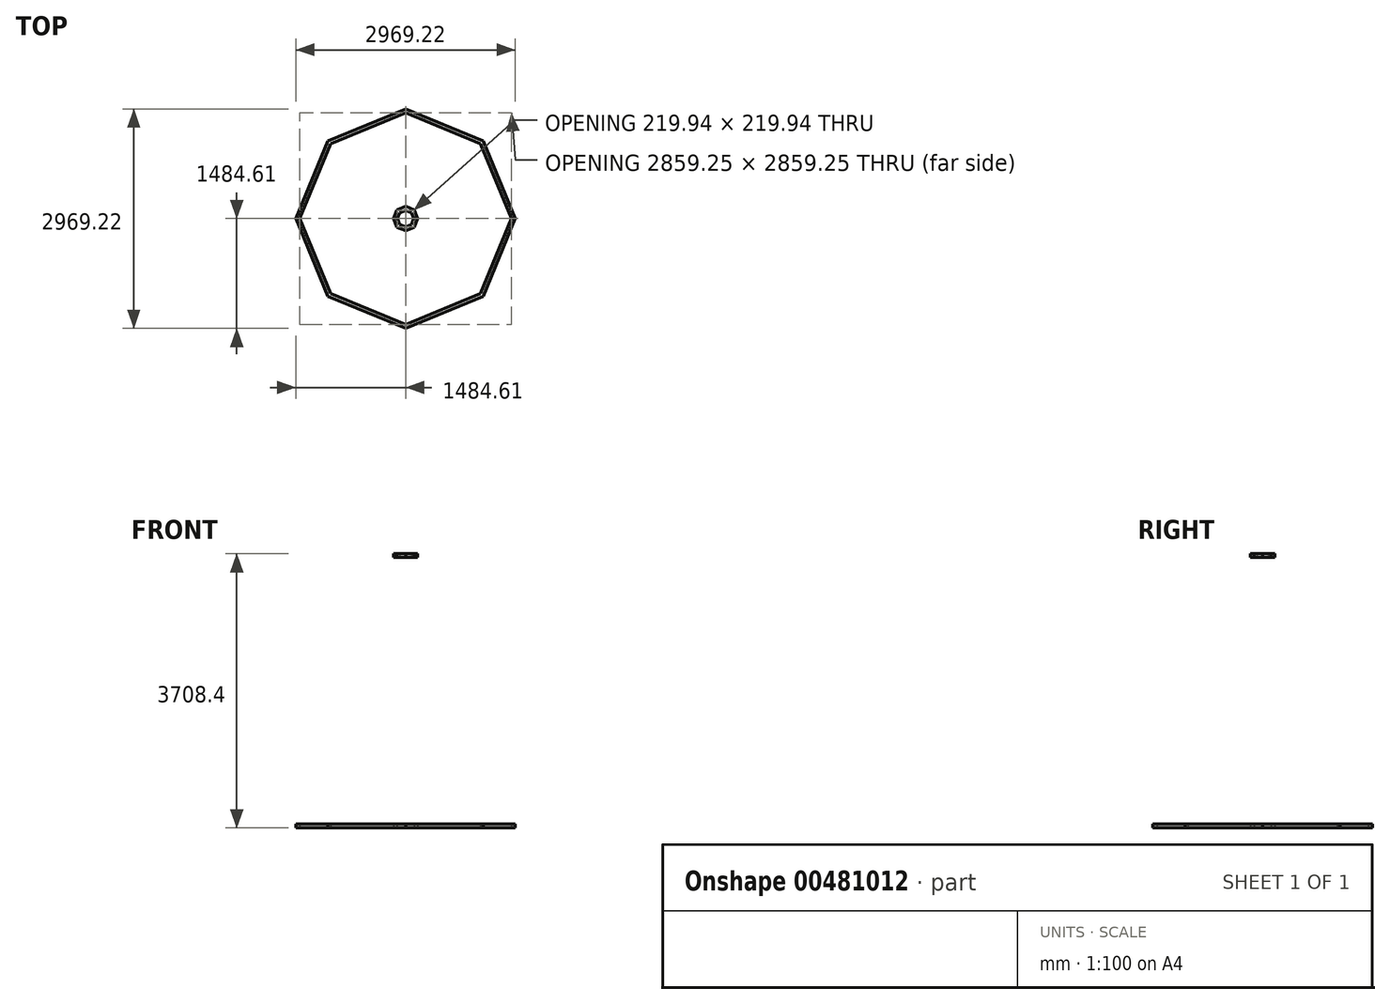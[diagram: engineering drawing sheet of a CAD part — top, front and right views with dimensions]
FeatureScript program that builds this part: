
annotation { "Feature Type Name" : "Feature", "Feature Type Description" : "" }
export const myFeature = defineFeature(function(context is Context, id is Id, definition is map)
    precondition{}
    {
        {
            var Q0;
            Q0=qCreatedBy(makeId("Top.planeOp"),FACE);
            var sketch = newSketch(context, id + "F0", { "sketchPlane" : qUnion([Q0])});
            skCircle(sketch, "E0.cCircle", {"center": v(0, 0) * mm, "radius": 1371.6 * mm, "construction": true});
            skLineSegment(sketch, "E0.0", {"start": v(1484.6, 0) * mm, "end": v(1049.78, -1049.78) * mm});
            skLineSegment(sketch, "E0.1", {"start": v(1049.78, -1049.78) * mm, "end": v(0, -1484.6) * mm});
            skLineSegment(sketch, "E0.2", {"start": v(0, -1484.6) * mm, "end": v(-1049.78, -1049.78) * mm});
            skLineSegment(sketch, "E0.3", {"start": v(-1049.78, -1049.78) * mm, "end": v(-1484.6, 0) * mm});
            skLineSegment(sketch, "E0.4", {"start": v(-1484.6, 0) * mm, "end": v(-1049.78, 1049.78) * mm});
            skLineSegment(sketch, "E0.5", {"start": v(-1049.78, 1049.78) * mm, "end": v(0, 1484.6) * mm});
            skLineSegment(sketch, "E0.6", {"start": v(0, 1484.6) * mm, "end": v(1049.78, 1049.78) * mm});
            skLineSegment(sketch, "E0.7", {"start": v(1049.78, 1049.78) * mm, "end": v(1484.6, 0) * mm});
            skPoint(sketch, "E0.0.midPoint", {"position": v(1267.2, -524.89) * mm});
            skLineSegment(sketch, "E1.0", {"start": v(-1429.62, 0) * mm, "end": v(-1010.9, 1010.9) * mm});
            skLineSegment(sketch, "E1.1", {"start": v(-1010.9, -1010.9) * mm, "end": v(-1429.62, 0) * mm});
            skLineSegment(sketch, "E1.2", {"start": v(-1010.9, 1010.9) * mm, "end": v(0, 1429.62) * mm});
            skLineSegment(sketch, "E1.3", {"start": v(0, -1429.62) * mm, "end": v(-1010.9, -1010.9) * mm});
            skLineSegment(sketch, "E1.4", {"start": v(0, 1429.62) * mm, "end": v(1010.9, 1010.9) * mm});
            skLineSegment(sketch, "E1.5", {"start": v(1010.9, 1010.9) * mm, "end": v(1429.62, 0) * mm});
            skLineSegment(sketch, "E1.6", {"start": v(1429.62, 0) * mm, "end": v(1010.9, -1010.9) * mm});
            skLineSegment(sketch, "E1.7", {"start": v(1010.9, -1010.9) * mm, "end": v(0, -1429.62) * mm});
            skSolve(sketch);
        }
        {
            var Q0;
            Q0 = qSketchRegion(id + "F0", true);
            extrude(context, id + "F1", {"entities" : qUnion([Q0]), "depth" : 50.8 * mm});
        }
        {
            var Q0;
            Q0=qCreatedBy(makeId("Top.planeOp"),FACE);
            cPlane(context, id + "F2", {"entities" : qUnion([Q0]), "cplaneType" : CPlaneType.OFFSET, "offset" : 3657.6 * mm, "width" : 152.4 * mm, "height" : 152.4 * mm});
        }
        {
            var Q0;
            Q0=qCreatedBy(id+"F2.planeOp",FACE);
            var sketch = newSketch(context, id + "F3", { "sketchPlane" : qUnion([Q0])});
            skCircle(sketch, "E2.cCircle", {"center": v(0, 0) * mm, "radius": 152.4 * mm, "construction": true});
            skLineSegment(sketch, "E2.0", {"start": v(164.96, 0) * mm, "end": v(116.64, -116.64) * mm});
            skLineSegment(sketch, "E2.1", {"start": v(116.64, -116.64) * mm, "end": v(0, -164.96) * mm});
            skLineSegment(sketch, "E2.2", {"start": v(0, -164.96) * mm, "end": v(-116.64, -116.64) * mm});
            skLineSegment(sketch, "E2.3", {"start": v(-116.64, -116.64) * mm, "end": v(-164.96, 0) * mm});
            skLineSegment(sketch, "E2.4", {"start": v(-164.96, 0) * mm, "end": v(-116.64, 116.64) * mm});
            skLineSegment(sketch, "E2.5", {"start": v(-116.64, 116.64) * mm, "end": v(0, 164.96) * mm});
            skLineSegment(sketch, "E2.6", {"start": v(0, 164.96) * mm, "end": v(116.64, 116.64) * mm});
            skLineSegment(sketch, "E2.7", {"start": v(116.64, 116.64) * mm, "end": v(164.96, 0) * mm});
            skPoint(sketch, "E2.0.midPoint", {"position": v(140.8, -58.32) * mm});
            skLineSegment(sketch, "E3.0", {"start": v(-109.97, 0) * mm, "end": v(-77.76, 77.76) * mm});
            skLineSegment(sketch, "E3.1", {"start": v(-77.76, -77.76) * mm, "end": v(-109.97, 0) * mm});
            skLineSegment(sketch, "E3.2", {"start": v(-77.76, 77.76) * mm, "end": v(0, 109.97) * mm});
            skLineSegment(sketch, "E3.3", {"start": v(0, -109.97) * mm, "end": v(-77.76, -77.76) * mm});
            skLineSegment(sketch, "E3.4", {"start": v(0, 109.97) * mm, "end": v(77.76, 77.76) * mm});
            skLineSegment(sketch, "E3.5", {"start": v(77.76, 77.76) * mm, "end": v(109.97, 0) * mm});
            skLineSegment(sketch, "E3.6", {"start": v(109.97, 0) * mm, "end": v(77.76, -77.76) * mm});
            skLineSegment(sketch, "E3.7", {"start": v(77.76, -77.76) * mm, "end": v(0, -109.97) * mm});
            skSolve(sketch);
        }
        {
            var Q0;
            Q0 = qSketchRegion(id + "F3", true);
            extrude(context, id + "F4", {"entities" : qUnion([Q0]), "depth" : 50.8 * mm});
        }
        {
            var Q0;
            Q0=qCreatedBy(makeId("Top.planeOp"),FACE);
            var sketch = newSketch(context, id + "F5", { "sketchPlane" : qUnion([Q0])});
            skCircle(sketch, "E4.cCircle", {"center": v(0, 0) * mm, "radius": 152.4 * mm, "construction": true});
            skLineSegment(sketch, "E4.0", {"start": v(164.96, 0) * mm, "end": v(116.64, -116.64) * mm});
            skLineSegment(sketch, "E4.1", {"start": v(116.64, -116.64) * mm, "end": v(0, -164.96) * mm});
            skLineSegment(sketch, "E4.2", {"start": v(0, -164.96) * mm, "end": v(-116.64, -116.64) * mm});
            skLineSegment(sketch, "E4.3", {"start": v(-116.64, -116.64) * mm, "end": v(-164.96, 0) * mm});
            skLineSegment(sketch, "E4.4", {"start": v(-164.96, 0) * mm, "end": v(-116.64, 116.64) * mm});
            skLineSegment(sketch, "E4.5", {"start": v(-116.64, 116.64) * mm, "end": v(0, 164.96) * mm});
            skLineSegment(sketch, "E4.6", {"start": v(0, 164.96) * mm, "end": v(116.64, 116.64) * mm});
            skLineSegment(sketch, "E4.7", {"start": v(116.64, 116.64) * mm, "end": v(164.96, 0) * mm});
            skPoint(sketch, "E4.0.midPoint", {"position": v(140.8, -58.32) * mm});
            skSolve(sketch);
        }
        {
            var Q0;
            Q0 = qSketchRegion(id + "F5", true);
            extrude(context, id + "F6", {"entities" : qUnion([Q0]), "depth" : 50.8 * mm});
        }
    });
